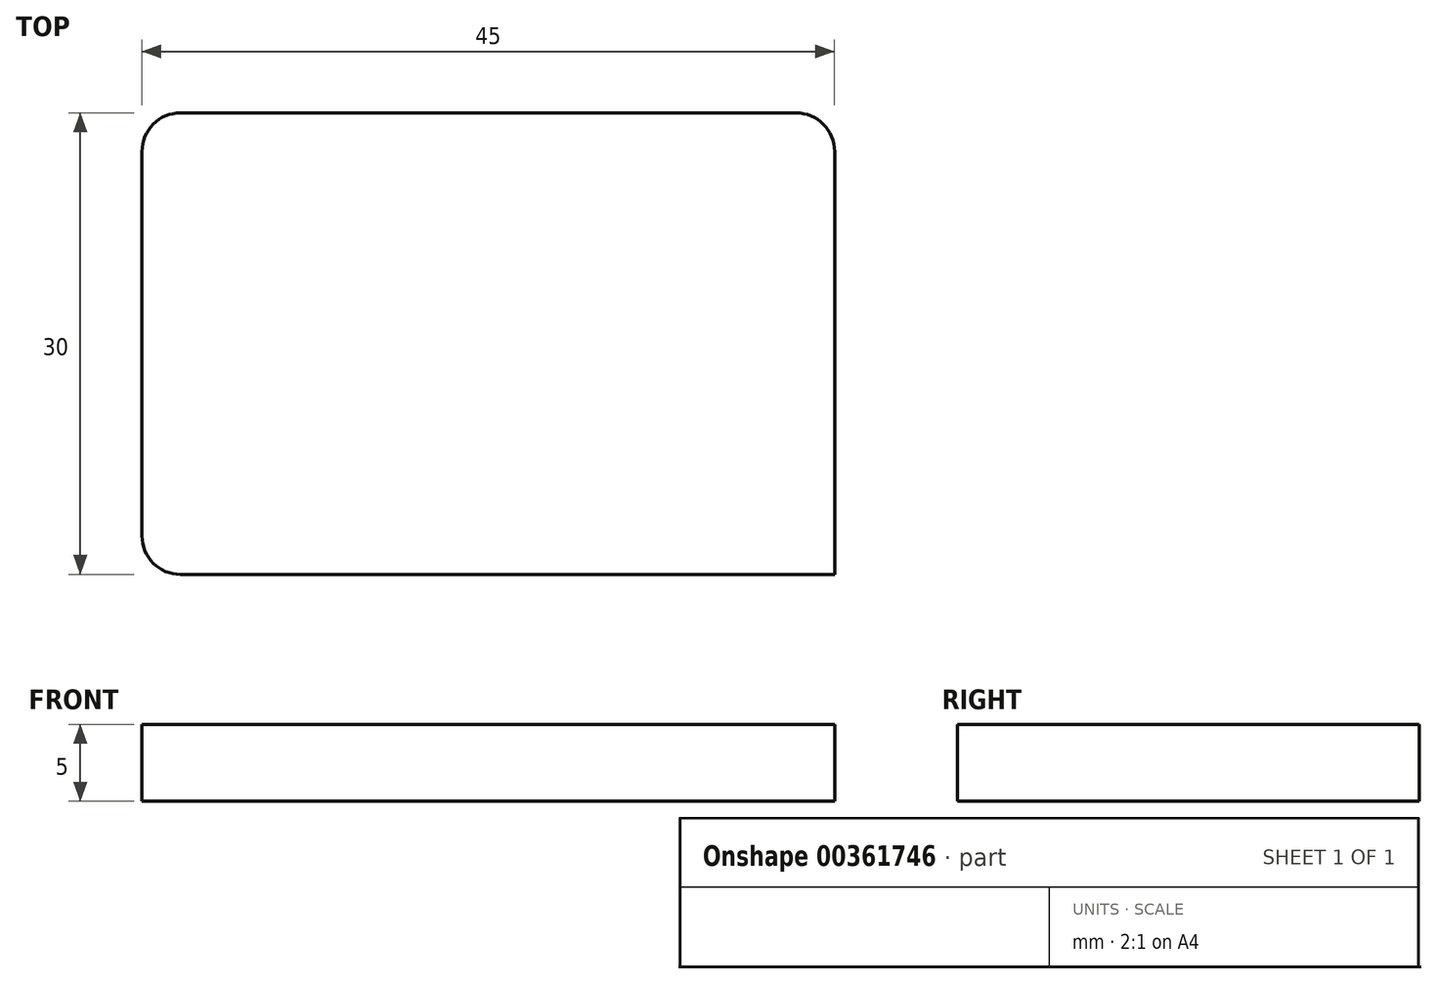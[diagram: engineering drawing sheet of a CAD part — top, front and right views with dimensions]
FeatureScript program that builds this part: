
annotation { "Feature Type Name" : "Feature", "Feature Type Description" : "" }
export const myFeature = defineFeature(function(context is Context, id is Id, definition is map)
    precondition{}
    {
        {
            var Q0;
            Q0=qCreatedBy(makeId("Top.planeOp"),FACE);
            var sketch = newSketch(context, id + "F0", { "sketchPlane" : qUnion([Q0])});
            skLineSegment(sketch, "E0.bottom", {"start": v(-19.86, 18.1) * mm, "end": v(25.14, 18.1) * mm});
            skLineSegment(sketch, "E0.top", {"start": v(-19.86, -11.9) * mm, "end": v(25.14, -11.9) * mm});
            skLineSegment(sketch, "E0.left", {"start": v(-19.86, 18.1) * mm, "end": v(-19.86, -11.9) * mm});
            skLineSegment(sketch, "E0.right", {"start": v(25.14, 18.1) * mm, "end": v(25.14, -11.9) * mm});
            skSolve(sketch);
        }
        {
            var Q0;
            Q0=makeQuery(id+"F0.imprint","IMPRINT",FACE,{"disambiguationData":[TD([[makeQuery(id+"F0.imprint","IMPRINT",EDGE,{"derivedFrom":sQuery(id+"F0.wireOp",EDGE,"E0.bottom")}),-1.0]])]});
            extrude(context, id + "F1", {"entities" : qUnion([Q0]), "depth" : 5 * mm});
        }
        {
            var Q0;
            Q0=makeQuery(id+"F1.opExtrude","SWEPT_EDGE",EDGE,{"disambiguationData":[OSD([sQuery(id+"F0.wireOp",EDGE,"E0.top"),sQuery(id+"F0.wireOp",EDGE,"E0.left")])]});
            var Q1;
            Q1=makeQuery(id+"F1.opExtrude","SWEPT_EDGE",EDGE,{"disambiguationData":[OSD([sQuery(id+"F0.wireOp",EDGE,"E0.bottom"),sQuery(id+"F0.wireOp",EDGE,"E0.left")])]});
            var Q2;
            Q2=makeQuery(id+"F1.opExtrude","SWEPT_EDGE",EDGE,{"disambiguationData":[OSD([sQuery(id+"F0.wireOp",EDGE,"E0.bottom"),sQuery(id+"F0.wireOp",EDGE,"E0.right")])]});
            fillet(context, id + "F2", {"entities" : qUnion([Q0, Q1, Q2]), "radius" : 2.5 * mm, "tangentPropagation" : true, "allowEdgeOverflow" : false});
        }
    });
